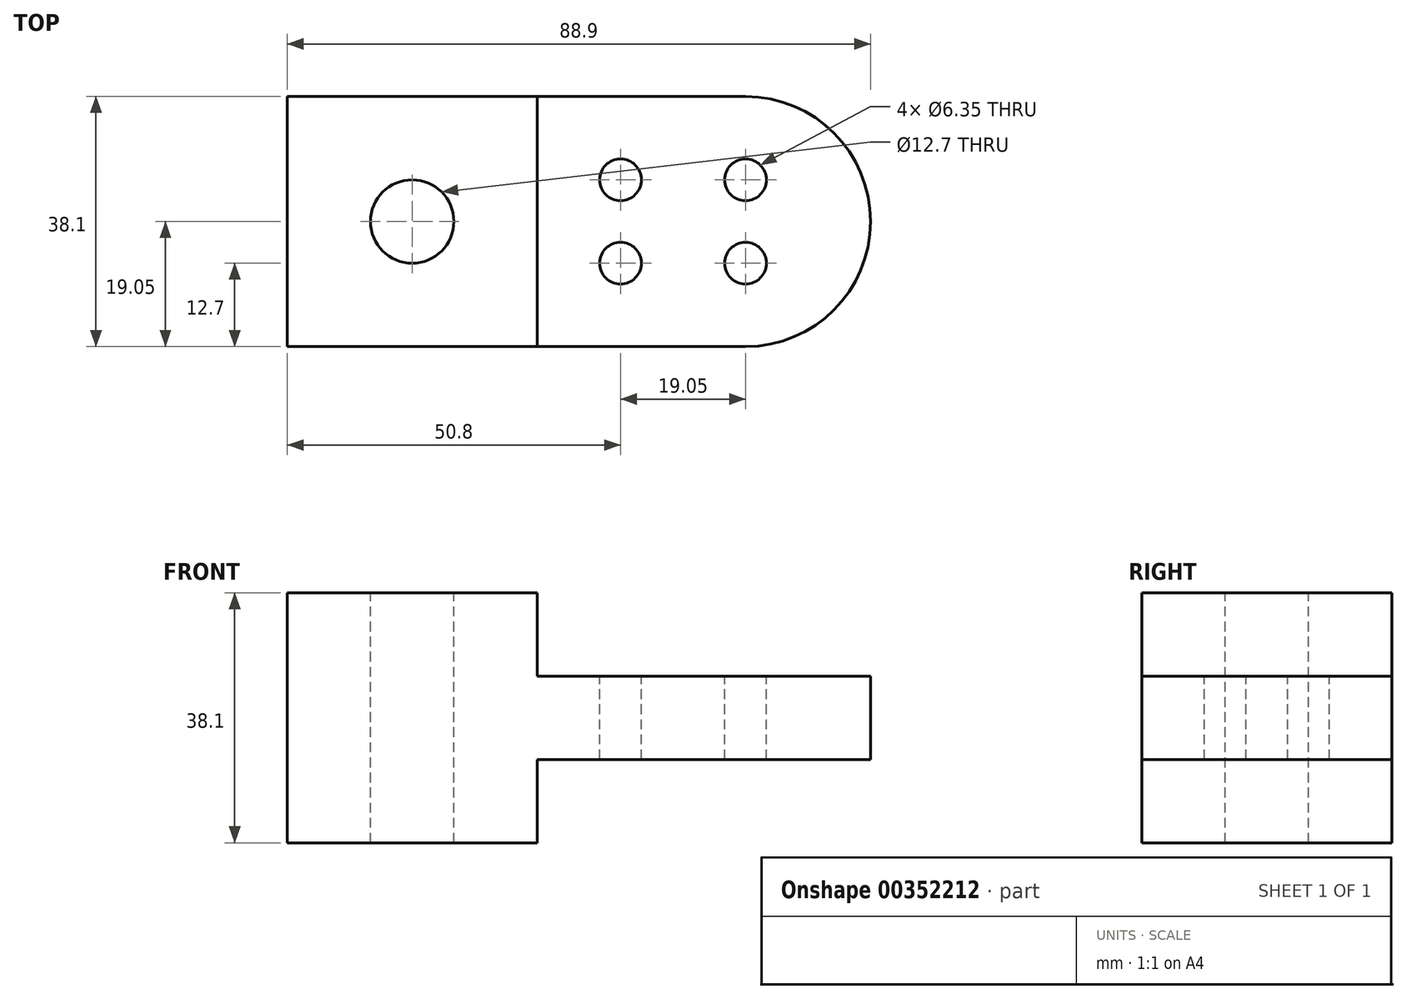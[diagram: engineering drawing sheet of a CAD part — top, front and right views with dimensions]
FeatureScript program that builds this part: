
annotation { "Feature Type Name" : "Feature", "Feature Type Description" : "" }
export const myFeature = defineFeature(function(context is Context, id is Id, definition is map)
    precondition{}
    {
        {
            var Q0;
            Q0=qCreatedBy(makeId("Front.planeOp"),FACE);
            var sketch = newSketch(context, id + "F0", { "sketchPlane" : qUnion([Q0])});
            skLineSegment(sketch, "E0", {"start": v(0, 0) * mm, "end": v(0, 38.1) * mm});
            skLineSegment(sketch, "E1", {"start": v(0, 38.1) * mm, "end": v(38.1, 38.1) * mm});
            skLineSegment(sketch, "E2", {"start": v(38.1, 38.1) * mm, "end": v(38.1, 25.4) * mm});
            skLineSegment(sketch, "E3", {"start": v(38.1, 25.4) * mm, "end": v(88.9, 25.4) * mm});
            skLineSegment(sketch, "E4", {"start": v(88.9, 25.4) * mm, "end": v(88.9, 12.7) * mm});
            skLineSegment(sketch, "E5", {"start": v(88.9, 12.7) * mm, "end": v(38.1, 12.7) * mm});
            skLineSegment(sketch, "E6", {"start": v(38.1, 12.7) * mm, "end": v(38.1, 0) * mm});
            skLineSegment(sketch, "E7", {"start": v(38.1, 0) * mm, "end": v(0, 0) * mm});
            skSolve(sketch);
        }
        {
            var Q0;
            Q0 = qSketchRegion(id + "F0", true);
            extrude(context, id + "F1", {"entities" : qUnion([Q0]), "depth" : 38.1 * mm});
        }
        {
            var Q0;
            Q0=makeQuery(id+"F1.opExtrude","CAP_EDGE",EDGE,{"disambiguationData":[OSD([sQuery(id+"F0.wireOp",EDGE,"E4")])],"isStart":false});
            var Q1;
            Q1=makeQuery(id+"F1.opExtrude","CAP_EDGE",EDGE,{"disambiguationData":[OSD([sQuery(id+"F0.wireOp",EDGE,"E4")])],"isStart":true});
            fillet(context, id + "F2", {"entities" : qUnion([Q0, Q1]), "radius" : 19.05 * mm, "tangentPropagation" : true, "allowEdgeOverflow" : false});
        }
        {
            var Q0;
            Q0=makeQuery(id+"F1.opExtrude","SWEPT_FACE",FACE,{"disambiguationData":[OSD([sQuery(id+"F0.wireOp",EDGE,"E1")])]});
            var sketch = newSketch(context, id + "F3", { "sketchPlane" : qUnion([Q0])});
            skCircle(sketch, "E8", {"center": v(19.05, -19.05) * mm, "radius": 6.35 * mm});
            skLineSegment(sketch, "E9", {"start": v(-10.71, -19.05) * mm, "end": v(105.7, -19.05) * mm, "construction": true});
            skPoint(sketch, "E9.startSnap0", {"position": v(0, -19.05) * mm});
            skPoint(sketch, "E9.endSnap0", {"position": v(38.1, -19.05) * mm});
            skCircle(sketch, "E10", {"center": v(50.8, -12.7) * mm, "radius": 3.18 * mm});
            skCircle(sketch, "E11", {"center": v(69.85, -12.7) * mm, "radius": 3.18 * mm});
            skCircle(sketch, "E12", {"center": v(50.8, -25.4) * mm, "radius": 3.18 * mm});
            skCircle(sketch, "E13", {"center": v(69.85, -25.4) * mm, "radius": 3.18 * mm});
            skSolve(sketch);
        }
        {
            var Q0;
            Q0 = qSketchRegion(id + "F3", true);
            extrude(context, id + "F4", {"entities" : qUnion([Q0]), "operationType" : NewBodyOperationType.REMOVE, "endBound" : BoundingType.THROUGH_ALL, "oppositeDirection" : true, "depth" : 25.4 * mm});
        }
    });
